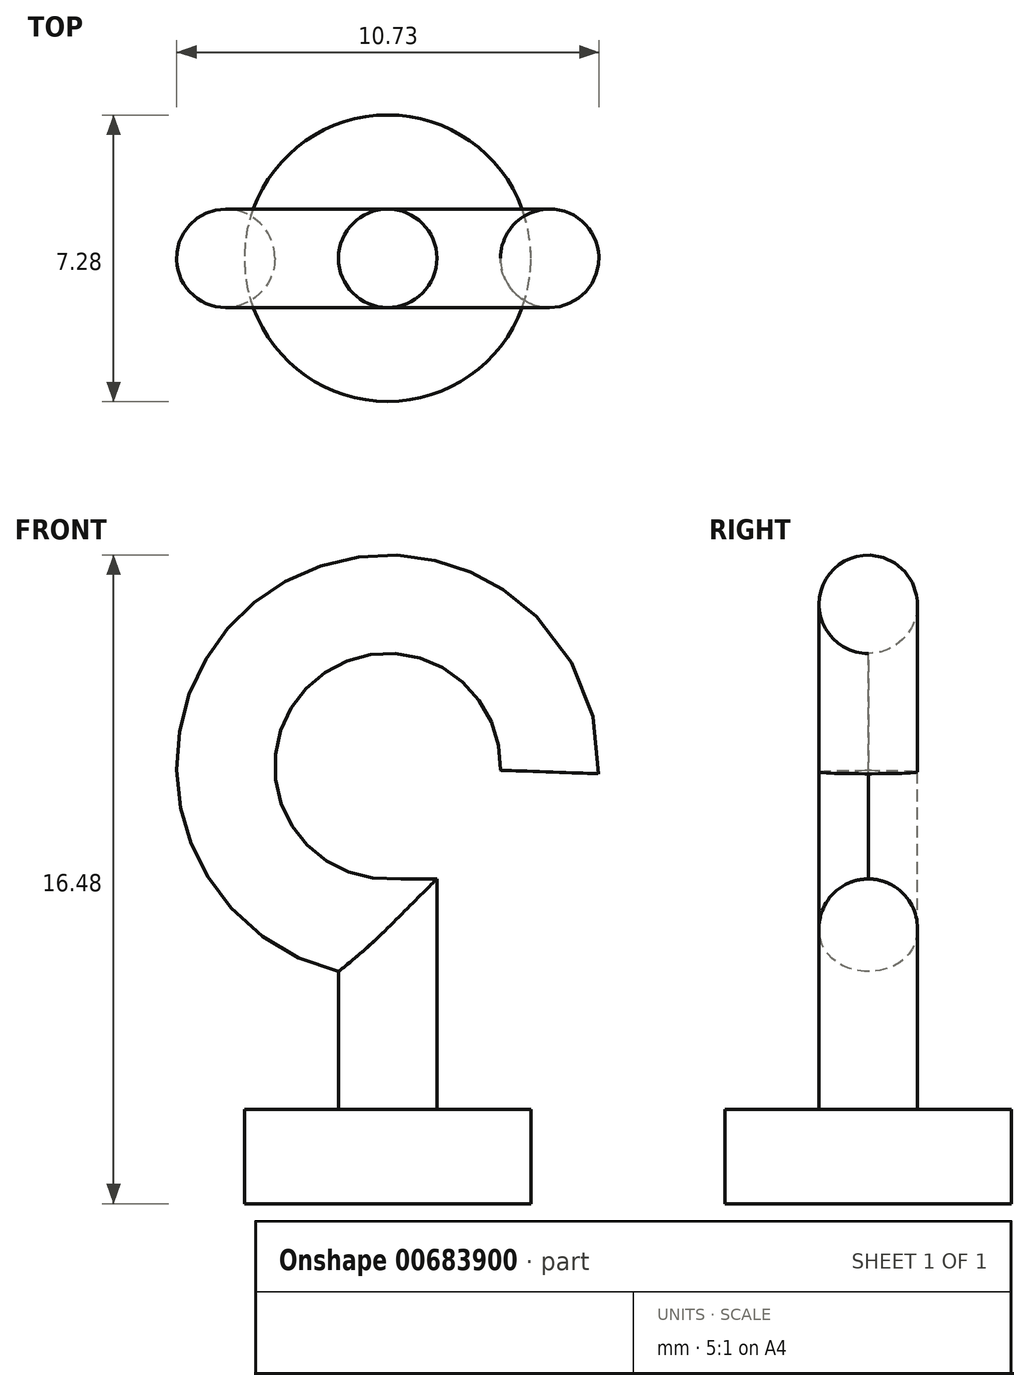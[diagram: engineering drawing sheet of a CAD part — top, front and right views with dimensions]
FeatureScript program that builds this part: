
annotation { "Feature Type Name" : "Feature", "Feature Type Description" : "" }
export const myFeature = defineFeature(function(context is Context, id is Id, definition is map)
    precondition{}
    {
        {
            var Q0;
            Q0=qCreatedBy(makeId("Top.planeOp"),FACE);
            var sketch = newSketch(context, id + "F0", { "sketchPlane" : qUnion([Q0])});
            skCircle(sketch, "E0", {"center": v(0, 0) * mm, "radius": 1.25 * mm});
            skSolve(sketch);
        }
        {
            var Q0;
            Q0=qCreatedBy(makeId("Front.planeOp"),FACE);
            var sketch = newSketch(context, id + "F1", { "sketchPlane" : qUnion([Q0])});
            skLineSegment(sketch, "E1", {"start": v(0, 0) * mm, "end": v(0, 7) * mm});
            skArc(sketch, "E2", {"start": v(4.11, 10.97) * mm, "mid": v(-2.86, 14.08) * mm, "end": v(0, 7) * mm});
            skSolve(sketch);
        }
        {
            var Q0;
            Q0=makeQuery(id+"F0.imprint","IMPRINT",FACE,{"disambiguationData":[TD([[makeQuery(id+"F0.imprint","IMPRINT",EDGE,{"derivedFrom":sQuery(id+"F0.wireOp",EDGE,"E0")}),1.0]])]});
            var Q1;
            Q1 = qSketchRegion(id + "F1", true);
            var Q2;
            Q2 = qConstructionFilter(qBodyType(qCreatedBy(id + "F1" ,EDGE), BodyType.WIRE), ConstructionObject.NO);
            sweep(context, id + "F2", {"profiles" : qUnion([Q0, Q1]), "path" : qUnion([Q2])});
        }
        {
            var Q0;
            Q0=qCreatedBy(makeId("Top.planeOp"),FACE);
            var sketch = newSketch(context, id + "F3", { "sketchPlane" : qUnion([Q0])});
            skCircle(sketch, "E3", {"center": v(0, 0) * mm, "radius": 3.64 * mm});
            skSolve(sketch);
        }
        {
            var Q0;
            Q0 = qSketchRegion(id + "F3", true);
            extrude(context, id + "F4", {"entities" : qUnion([Q0]), "operationType" : NewBodyOperationType.ADD, "depth" : 2.4 * mm, "offsetDistance" : 25 * mm});
        }
    });
